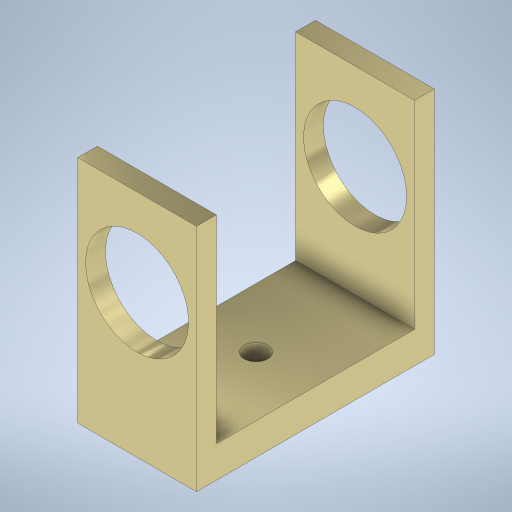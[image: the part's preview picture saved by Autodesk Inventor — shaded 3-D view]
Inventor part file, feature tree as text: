
AUTODESK INVENTOR PART (.ipt)
format: ipt  version: 2024 (Build 280153000, 153)  size: 279,552 bytes
history: native  units: mm
features: extrude x4, sketch x4
ambient origin geometry x8: Origin, YZ Plane, XZ Plane, XY Plane, X Axis, Y Axis, Z Axis, Center Point
bodies: Solid1 (feature_tree)
feature tree (8):
  extrude  "Extrusion1"  Depth=30.0mm
  extrude  "Extrusion2"  Depth=2.5mm
  extrude  "Extrusion4"  Depth=25.0mm
  extrude  "Extrusion5"  Depth=30.0mm
  sketch  "Sketch1"  dims[d0=15.0mm d1=30.0mm]
  sketch  "Sketch2"  dims[d2=4.0mm d3=0.0mm d4=2.5mm]
  sketch  "Sketch4"  dims[d5=25.0mm d6=0.0mm d12=7.0mm]
  sketch  "Sketch5"  dims[d13=13.0mm d14=5.984189mm d15=30.0mm d16=0.0mm d17=3.0mm d18=5.0mm d19=0.0mm d11=0.5mm]
